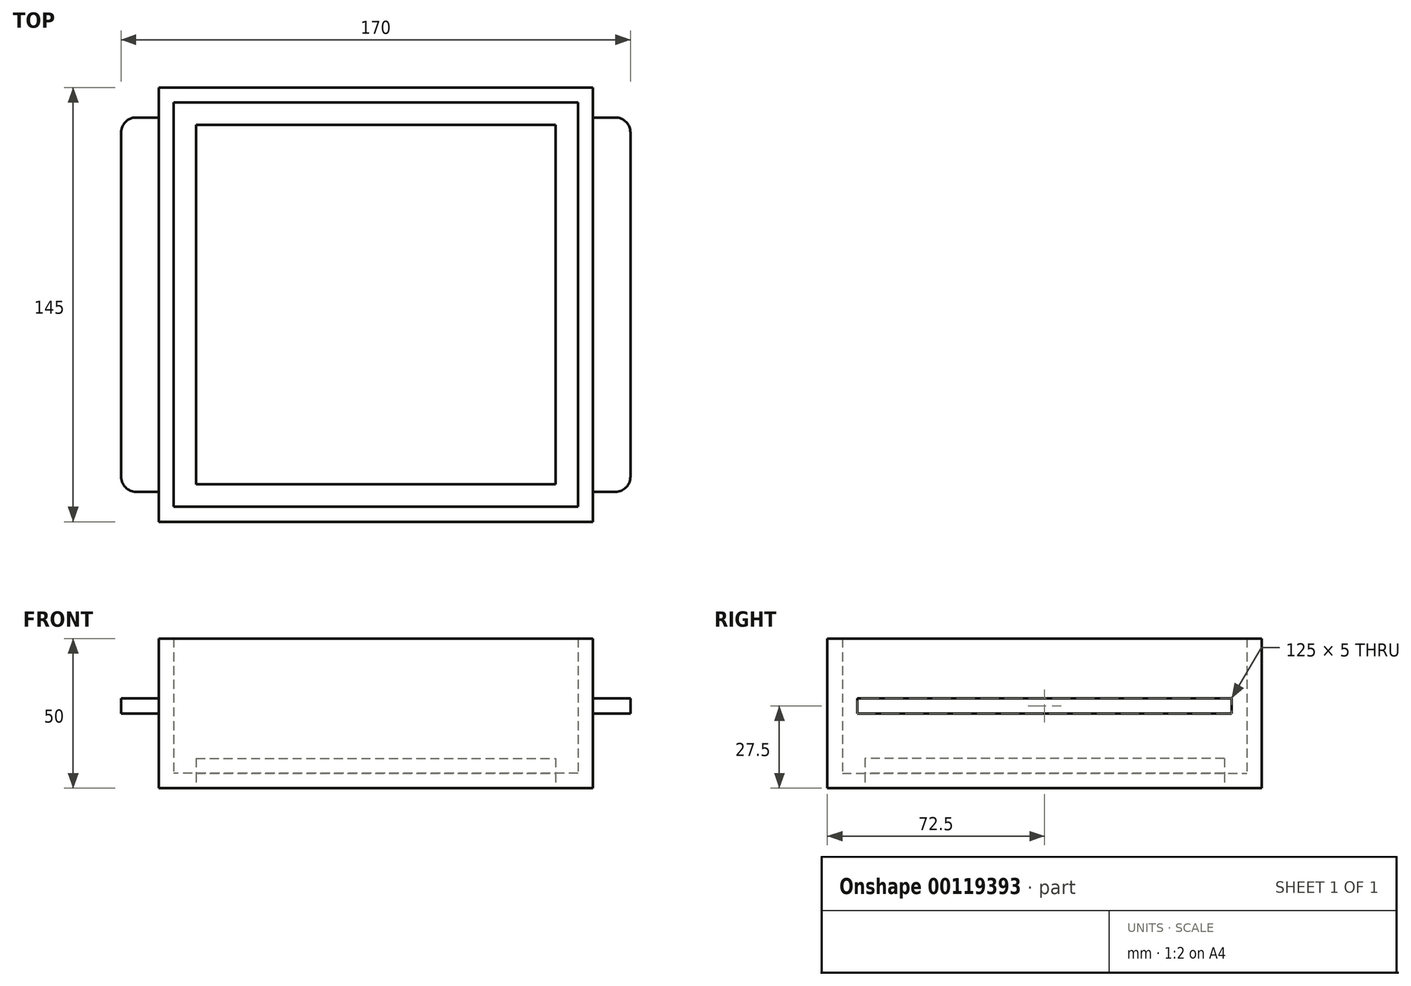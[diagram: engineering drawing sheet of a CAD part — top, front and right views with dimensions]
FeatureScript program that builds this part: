
annotation { "Feature Type Name" : "Feature", "Feature Type Description" : "" }
export const myFeature = defineFeature(function(context is Context, id is Id, definition is map)
    precondition{}
    {
        {
            var Q0;
            Q0=qCreatedBy(makeId("Top.planeOp"),FACE);
            var sketch = newSketch(context, id + "F0", { "sketchPlane" : qUnion([Q0])});
            skLineSegment(sketch, "E0.bottom", {"start": v(72.5, -72.5) * mm, "end": v(-72.5, -72.5) * mm});
            skLineSegment(sketch, "E0.top", {"start": v(72.5, 72.5) * mm, "end": v(-72.5, 72.5) * mm});
            skLineSegment(sketch, "E0.left", {"start": v(72.5, -72.5) * mm, "end": v(72.5, 72.5) * mm});
            skLineSegment(sketch, "E0.right", {"start": v(-72.5, -72.5) * mm, "end": v(-72.5, 72.5) * mm});
            skPoint(sketch, "E0.middle", {"position": v(0, 0) * mm});
            skSolve(sketch);
        }
        {
            var Q0;
            Q0=makeQuery(id+"F0.imprint","IMPRINT",FACE,{"disambiguationData":[TD([[makeQuery(id+"F0.imprint","IMPRINT",EDGE,{"derivedFrom":sQuery(id+"F0.wireOp",EDGE,"E0.bottom")}),-1.0]])]});
            extrude(context, id + "F1", {"entities" : qUnion([Q0]), "depth" : 50 * mm});
        }
        {
            var Q0;
            Q0=makeQuery(id+"F1.opExtrude","CAP_FACE",FACE,{"disambiguationData":[OSD([sQuery(id+"F0.wireOp",EDGE,"E0.bottom"),sQuery(id+"F0.wireOp",EDGE,"E0.top"),sQuery(id+"F0.wireOp",EDGE,"E0.left"),sQuery(id+"F0.wireOp",EDGE,"E0.right")])],"isStart":false});
            shell(context, id + "F2", {"entities" : qUnion([Q0]), "thickness" : 5 * mm});
        }
        {
            var Q0;
            Q0=qCreatedBy(makeId("Top.planeOp"),FACE);
            var sketch = newSketch(context, id + "F3", { "sketchPlane" : qUnion([Q0])});
            skLineSegment(sketch, "E1.bottom", {"start": v(60, -60) * mm, "end": v(-60, -60) * mm});
            skLineSegment(sketch, "E1.top", {"start": v(60, 60) * mm, "end": v(-60, 60) * mm});
            skLineSegment(sketch, "E1.left", {"start": v(60, -60) * mm, "end": v(60, 60) * mm});
            skLineSegment(sketch, "E1.right", {"start": v(-60, -60) * mm, "end": v(-60, 60) * mm});
            skPoint(sketch, "E1.middle", {"position": v(0, 0) * mm});
            skSolve(sketch);
        }
        {
            var Q0;
            Q0 = qSketchRegion(id + "F3", true);
            extrude(context, id + "F4", {"entities" : qUnion([Q0]), "operationType" : NewBodyOperationType.REMOVE, "depth" : 25 * mm});
        }
        {
            var Q0;
            Q0=qCreatedBy(makeId("Top.planeOp"),FACE);
            cPlane(context, id + "F5", {"entities" : qUnion([Q0]), "cplaneType" : CPlaneType.OFFSET, "offset" : 25 * mm, "width" : 150 * mm, "height" : 150 * mm});
        }
        {
            var Q0;
            Q0=qCreatedBy(id+"F5.planeOp",FACE);
            var sketch = newSketch(context, id + "F6", { "sketchPlane" : qUnion([Q0])});
            skLineSegment(sketch, "E2.bottom", {"start": v(-70, 62.5) * mm, "end": v(-85, 62.5) * mm});
            skLineSegment(sketch, "E2.top", {"start": v(-70, -62.5) * mm, "end": v(-85, -62.5) * mm});
            skLineSegment(sketch, "E2.left", {"start": v(-70, 62.5) * mm, "end": v(-70, -62.5) * mm});
            skLineSegment(sketch, "E2.right", {"start": v(-85, 62.5) * mm, "end": v(-85, -62.5) * mm});
            skLineSegment(sketch, "E3.bottom", {"start": v(70, 62.5) * mm, "end": v(85, 62.5) * mm});
            skLineSegment(sketch, "E3.top", {"start": v(70, -62.5) * mm, "end": v(85, -62.5) * mm});
            skLineSegment(sketch, "E3.left", {"start": v(70, 62.5) * mm, "end": v(70, -62.5) * mm});
            skLineSegment(sketch, "E3.right", {"start": v(85, 62.5) * mm, "end": v(85, -62.5) * mm});
            skSolve(sketch);
        }
        {
            var Q0;
            Q0 = qSketchRegion(id + "F6", true);
            extrude(context, id + "F7", {"entities" : qUnion([Q0]), "operationType" : NewBodyOperationType.ADD, "depth" : 5 * mm});
        }
        {
            var Q0;
            Q0=makeQuery(id+"F7.opExtrude","SWEPT_EDGE",EDGE,{"disambiguationData":[OSD([sQuery(id+"F6.wireOp",EDGE,"E2.bottom"),sQuery(id+"F6.wireOp",EDGE,"E2.right")])]});
            var Q1;
            Q1=makeQuery(id+"F7.opExtrude","SWEPT_EDGE",EDGE,{"disambiguationData":[OSD([sQuery(id+"F6.wireOp",EDGE,"E3.bottom"),sQuery(id+"F6.wireOp",EDGE,"E3.right")])]});
            var Q2;
            Q2=makeQuery(id+"F7.opExtrude","SWEPT_EDGE",EDGE,{"disambiguationData":[OSD([sQuery(id+"F6.wireOp",EDGE,"E3.top"),sQuery(id+"F6.wireOp",EDGE,"E3.right")])]});
            var Q3;
            Q3=makeQuery(id+"F7.opExtrude","SWEPT_EDGE",EDGE,{"disambiguationData":[OSD([sQuery(id+"F6.wireOp",EDGE,"E2.top"),sQuery(id+"F6.wireOp",EDGE,"E2.right")])]});
            fillet(context, id + "F8", {"entities" : qUnion([Q0, Q1, Q2, Q3]), "radius" : 5 * mm, "tangentPropagation" : true, "allowEdgeOverflow" : false});
        }
        {
            var Q0;
            Q0=makeQuery(id+"F2.opShell","OFFSET_FACE",FACE,{"disambiguationData":[OSD([sQuery(id+"F0.wireOp",EDGE,"E0.bottom"),sQuery(id+"F0.wireOp",EDGE,"E0.top"),sQuery(id+"F0.wireOp",EDGE,"E0.left"),sQuery(id+"F0.wireOp",EDGE,"E0.right")])]});
            var sketch = newSketch(context, id + "F9", { "sketchPlane" : qUnion([Q0])});
            skLineSegment(sketch, "E4.bottom", {"start": v(67.5, -67.5) * mm, "end": v(-67.5, -67.5) * mm});
            skLineSegment(sketch, "E4.top", {"start": v(67.5, 67.5) * mm, "end": v(-67.5, 67.5) * mm});
            skLineSegment(sketch, "E4.left", {"start": v(67.5, -67.5) * mm, "end": v(67.5, 67.5) * mm});
            skLineSegment(sketch, "E4.right", {"start": v(-67.5, -67.5) * mm, "end": v(-67.5, 67.5) * mm});
            skPoint(sketch, "E4.middle", {"position": v(0, 0) * mm});
            skSolve(sketch);
        }
        {
            var Q0;
            {var subQ0=makeQuery(id+"F2.opShell","OFFSET_FACE",FACE,{"disambiguationData":[OSD([sQuery(id+"F0.wireOp",EDGE,"E0.bottom"),sQuery(id+"F0.wireOp",EDGE,"E0.top"),sQuery(id+"F0.wireOp",EDGE,"E0.left"),sQuery(id+"F0.wireOp",EDGE,"E0.right")])]});Q0=makeQuery(id+"F9.imprint","IMPRINT",FACE,{"disambiguationData":[TD([[makeQuery(id+"F9.imprint","IMPRINT",EDGE,{"derivedFrom":makeQuery(id+"F4.boolean.opBoolean","INTERSECT",EDGE,{"derivedFrom":[subQ0,makeQuery(id+"F4.opExtrude","SWEPT_FACE",FACE,{"disambiguationData":[OSD([sQuery(id+"F3.wireOp",EDGE,"E1.bottom")])]})]})}),1.0]])]});}
            extrude(context, id + "F10", {"entities" : qUnion([Q0]), "depth" : 5 * mm});
        }
    });
